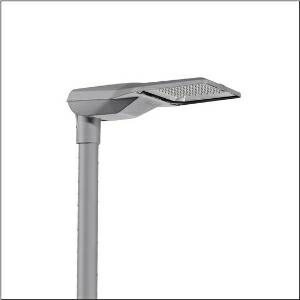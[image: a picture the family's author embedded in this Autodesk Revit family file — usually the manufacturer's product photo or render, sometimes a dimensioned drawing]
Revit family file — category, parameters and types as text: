
# Revit family: streetlight_sl_21_iq_midi___stw1_0a_5xe3e31d08nb_8d25
name_source: partatom
category: Lighting Fixtures
units: mm (PartAtom-declared; Revit-internal decimal feet)

## family parameters
Cut with Voids When Loaded = No
Host = Face
Light Source = No
Part Type = Normal
Room Calculation Point = No
Round Connector Dimension = Use Diameter
Shared = No

## types (1)
- --- (1 x LED, 23230 lm, 155.5 W, 3000K)
    Apparent Load = 155 VA
    CIE Flux Codes = 39 75 98 100 100
    Color Rendering = 70
    Color Temperature = 3000K
    Default Elevation = 1800 mm
    Description = Streetlight SL 21 iQ midi, mast luminaire, primary light control with lens, of PMMA, primary optical cover: cover, of toughened safety glass, transparent, light distribution: STW1.0a, light emission: direct distribution, primary light characteristic: asymmetric, installation type: post-top, side-entry, LED, High Power LED, rated luminous flux: 23.230lm, luminous efficacy: 149lm/W, light colour: 730, colour temperature: 3000K, control gear: iQ-Comfort, control: Auto-Match, Temp-Guard, Lumen-Switch, Night-Set, Smart-Wire, Light-Fading, Desk-Remote (wireless, voltage-free reading and setting of iQ features in the workshop via application-optimized NFC function/RFID function), optimised constant luminous flux control (CLO 2.0), pre-setting: linear dimming characteristic, mains connection: 230..240V, AC, 50/60Hz, start of lifetime: 156W, end of service life: 162W, reduction: 69W, luminaire housing, of diecast aluminium, powder-coated, Siteco® metallic grey (DB 702S), corrosivity category C5 mid according to DIN EN ISO 12944, please order mast flange separately, inclination adjustable: 0°, 5°, 10°, 15°, sealing non-destructively replaceable, multi-level sealing system, length: 644mm, width: 335mm, height: 110mm, mast flange for spigot size: 42mm (side-entry): 5XC10008XM4, 60/48mm (side-entry/post-top): 5XC10108XM2, 76/60mm (side-entry/post-top): 5XC10108XM1, mounting height: 4..8m, protection rating (complete): IP66, insulation class (complete): insulation class II (safety insulation), certification: CE, ENEC, ENEC+, VDE, impact resistance: IK10, permissible operating ambient temperature for outdoor applications: -40..+50°C, standard-compliant lighting for roads and squares, packaging unit: 1 piece

Light Distribution: STW1.0a
    Height = 111 mm
    Lamp = 1 x LED
    Lamp Light Flux = 23230 lm
    Lamp Power = 155.5 W
    Lamp count = 1
    Length = 644 mm
    Luminous efficacy = 149 lm/W
    Manufacturer = Siteco
    ModVariant = No
    Model = 5XE3E31D08NB
    Number of Poles = 1
    OnlyDefault = Yes
    Power Factor = 1
    Product Name = Streetlight SL 21 iQ midi | STW1.0a
    Product group = mast luminaire | pylon top
    ProductGroupID = 6100
    Protection Class = Protection class II
    Protection Degree = IP 66
    RLX_Detail_Level = 1
    RLX_Emergency_Light_Flux = 0 lm
    RLX_Emergency_Type = 0
    RLX_Emergency_Type_DB = No
    RlxData = <blob elided: 27305 chars, md5=2e1492cf>
    Socket = socket
    Standby Power = 0 W
    System Light Flux = 23230 lm
    System Power = 155 W
    Type Comments = factory setting: luminous flux: 100 % | dim-lin: 254 | 823 mA
    Type Image = l_1004298.jpg
    URL = http://relux.com
    VarID = @adj_191389
    Voltage = 0 V
    Weight = 0.00 kg
    Width = 336 mm

## geometry (parser evidence)
native form markers: Blend x4, Sweep x11
no freeform markers — native parametric forms only
